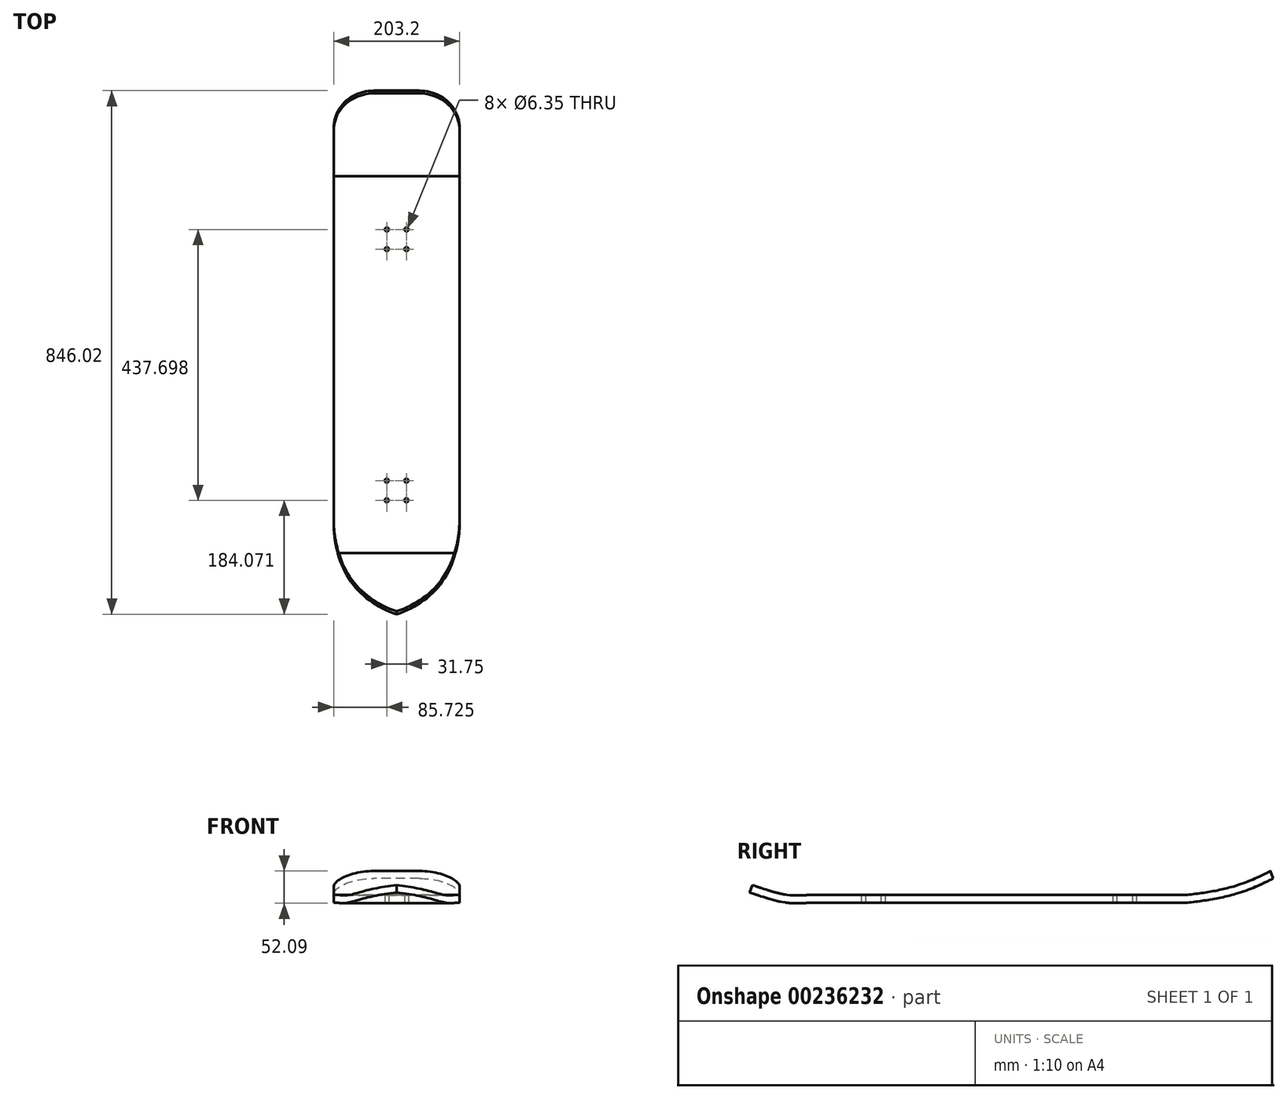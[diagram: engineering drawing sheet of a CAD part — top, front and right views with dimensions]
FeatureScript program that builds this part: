
annotation { "Feature Type Name" : "Feature", "Feature Type Description" : "" }
export const myFeature = defineFeature(function(context is Context, id is Id, definition is map)
    precondition{}
    {
        {
            var Q0;
            Q0=qCreatedBy(makeId("Top.planeOp"),FACE);
            var sketch = newSketch(context, id + "F0", { "sketchPlane" : qUnion([Q0])});
            skLineSegment(sketch, "E0.bottom", {"start": v(101.6, -304.8) * mm, "end": v(-101.6, -304.8) * mm});
            skLineSegment(sketch, "E0.top", {"start": v(101.6, 304.8) * mm, "end": v(-101.6, 304.8) * mm});
            skLineSegment(sketch, "E0.left", {"start": v(101.6, -304.8) * mm, "end": v(101.6, 304.8) * mm});
            skLineSegment(sketch, "E0.right", {"start": v(-101.6, -304.8) * mm, "end": v(-101.6, 304.8) * mm});
            skPoint(sketch, "E0.middle", {"position": v(0, 0) * mm});
            skPoint(sketch, "E1.middle", {"position": v(0, 202.97) * mm});
            skCircle(sketch, "E2", {"center": v(-15.87, 218.85) * mm, "radius": 3.18 * mm});
            skCircle(sketch, "E3", {"center": v(15.88, 218.85) * mm, "radius": 3.18 * mm});
            skCircle(sketch, "E4", {"center": v(-15.87, 187.1) * mm, "radius": 3.18 * mm});
            skCircle(sketch, "E5", {"center": v(15.88, 187.1) * mm, "radius": 3.18 * mm});
            skPoint(sketch, "E1.left.end.orphan", {"position": v(25.4, 228.37) * mm});
            skPoint(sketch, "E1.bottom.start.orphan", {"position": v(25.4, 177.57) * mm});
            skPoint(sketch, "E1.right.end.orphan", {"position": v(-25.4, 228.37) * mm});
            skPoint(sketch, "E1.right.start.orphan", {"position": v(-25.4, 177.57) * mm});
            skCircle(sketch, "E6.MirrorC", {"center": v(-15.87, -218.85) * mm, "radius": 3.18 * mm});
            skCircle(sketch, "E7.MirrorC", {"center": v(15.88, -218.85) * mm, "radius": 3.18 * mm});
            skCircle(sketch, "E8.MirrorC", {"center": v(15.88, -187.1) * mm, "radius": 3.18 * mm});
            skCircle(sketch, "E9.MirrorC", {"center": v(-15.87, -187.1) * mm, "radius": 3.18 * mm});
            skSolve(sketch);
        }
        {
            var Q0;
            Q0 = qSketchRegion(id + "F0", true);
            extrude(context, id + "F1", {"entities" : qUnion([Q0]), "endBound" : BoundingType.SYMMETRIC, "depth" : 12.7 * mm});
        }
        {
            var Q0;
            Q0=qCreatedBy(makeId("Right.planeOp"),FACE);
            var sketch = newSketch(context, id + "F2", { "sketchPlane" : qUnion([Q0])});
            skFitSpline(sketch, "E10", {"points": [v(304.63, 0) * mm, v(354.41, 7.4) * mm, v(403.6, 21.63) * mm, v(440.94, 38.82) * mm], "startDerivative": vector(144.25, 17.39) * mm, "endDerivative": vector(115.03, 57.78) * mm});
            skFitSpline(sketch, "E11", {"points": [v(-303.86, 0) * mm, v(-343.14, 0) * mm, v(-383.87, 10.55) * mm, v(-407.87, 18.55) * mm], "startDerivative": vector(-109.39, -7.7) * mm, "endDerivative": vector(-78.53, 26.4) * mm});
            skSolve(sketch);
        }
        {
            var Q0;
            Q0=makeQuery(id+"F1.opExtrude","SWEPT_FACE",FACE,{"disambiguationData":[OSD([sQuery(id+"F0.wireOp",EDGE,"E0.top")])]});
            var Q1;
            Q1=sQuery(id+"F2.wireOp",EDGE,"E10");
            sweep(context, id + "F3", {"operationType" : NewBodyOperationType.ADD, "profiles" : qUnion([Q0]), "path" : qUnion([Q1])});
        }
        {
            var Q0;
            Q0=makeQuery(id+"F1.opExtrude","SWEPT_FACE",FACE,{"disambiguationData":[OSD([sQuery(id+"F0.wireOp",EDGE,"E0.bottom")])]});
            var Q1;
            Q1=sQuery(id+"F2.wireOp",EDGE,"E11");
            sweep(context, id + "F4", {"operationType" : NewBodyOperationType.ADD, "profiles" : qUnion([Q0]), "path" : qUnion([Q1])});
        }
        {
            var Q0;
            Q0=makeQuery(id+"F4.opSweep","CAP_EDGE",EDGE,{"disambiguationData":[OSD([sQuery(id+"F0.wireOp",EDGE,"E0.bottom"),sQuery(id+"F0.wireOp",EDGE,"E0.right"),sQuery(id+"F2.wireOp",VERTEX,"E11.end")])],"isStart":false});
            var Q1;
            Q1=makeQuery(id+"F4.opSweep","CAP_EDGE",EDGE,{"disambiguationData":[OSD([sQuery(id+"F0.wireOp",EDGE,"E0.bottom"),sQuery(id+"F0.wireOp",EDGE,"E0.left"),sQuery(id+"F2.wireOp",VERTEX,"E11.end")])],"isStart":false});
            fillet(context, id + "F5", {"entities" : qUnion([Q0, Q1]), "radius" : 149 * mm, "tangentPropagation" : true, "allowEdgeOverflow" : false});
        }
        {
            var Q0;
            Q0=makeQuery(id+"F3.opSweep","CAP_EDGE",EDGE,{"disambiguationData":[OSD([sQuery(id+"F0.wireOp",EDGE,"E0.top"),sQuery(id+"F0.wireOp",EDGE,"E0.left"),sQuery(id+"F2.wireOp",VERTEX,"E10.end")])],"isStart":false});
            var Q1;
            Q1=makeQuery(id+"F3.opSweep","CAP_EDGE",EDGE,{"disambiguationData":[OSD([sQuery(id+"F0.wireOp",EDGE,"E0.top"),sQuery(id+"F0.wireOp",EDGE,"E0.right"),sQuery(id+"F2.wireOp",VERTEX,"E10.end")])],"isStart":false});
            fillet(context, id + "F6", {"entities" : qUnion([Q0, Q1]), "radius" : 65 * mm, "tangentPropagation" : true, "allowEdgeOverflow" : false});
        }
    });
